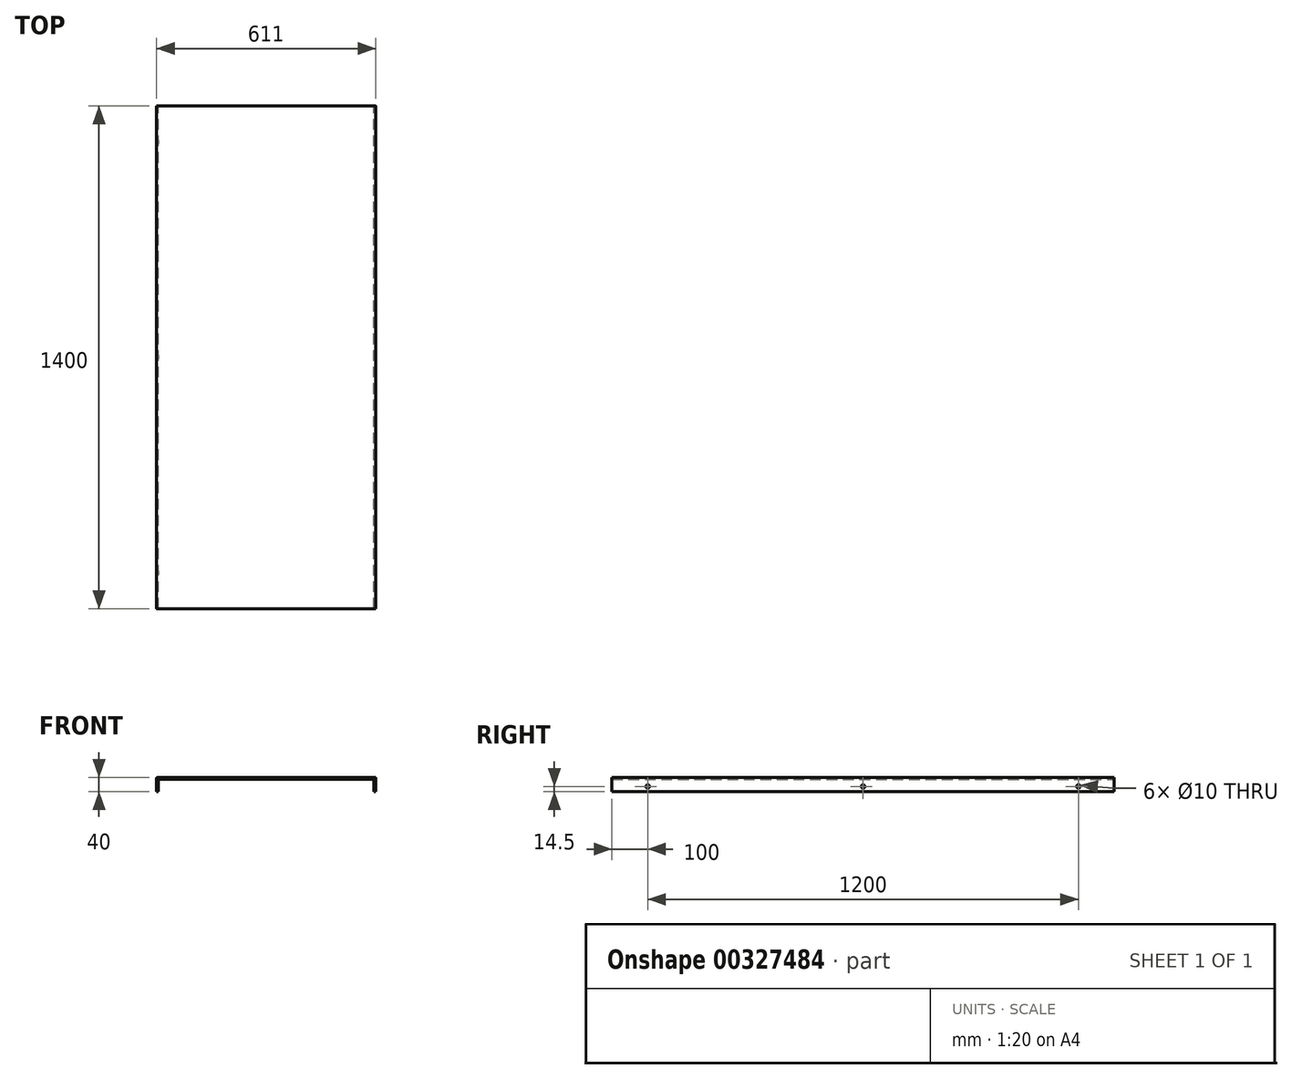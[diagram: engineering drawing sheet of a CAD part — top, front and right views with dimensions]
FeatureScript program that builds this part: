
annotation { "Feature Type Name" : "Feature", "Feature Type Description" : "" }
export const myFeature = defineFeature(function(context is Context, id is Id, definition is map)
    precondition{}
    {
        {
            var Q0;
            Q0=qCreatedBy(makeId("Front.planeOp"),FACE);
            var sketch = newSketch(context, id + "F0", { "sketchPlane" : qUnion([Q0])});
            skLineSegment(sketch, "E0", {"start": v(0, 0) * mm, "end": v(305.5, 0) * mm});
            skLineSegment(sketch, "E1", {"start": v(0, 0) * mm, "end": v(0, 40.14) * mm, "construction": true});
            skLineSegment(sketch, "E2.MirrorCS", {"start": v(0, 0) * mm, "end": v(-305.5, 0) * mm});
            skLineSegment(sketch, "E3", {"start": v(0, -5.5) * mm, "end": v(300, -5.5) * mm});
            skLineSegment(sketch, "E4", {"start": v(305.5, 0) * mm, "end": v(305.5, -40) * mm});
            skLineSegment(sketch, "E5.MirrorCS", {"start": v(-305.5, 0) * mm, "end": v(-305.5, -40) * mm});
            skLineSegment(sketch, "E6.MirrorCS", {"start": v(0, -5.5) * mm, "end": v(-300, -5.5) * mm});
            skLineSegment(sketch, "E7", {"start": v(300, -14.07) * mm, "end": v(300, -5.5) * mm});
            skLineSegment(sketch, "E8", {"start": v(300, -14.07) * mm, "end": v(300, -40) * mm});
            skLineSegment(sketch, "E9", {"start": v(305.5, -40) * mm, "end": v(300, -40) * mm});
            skLineSegment(sketch, "E10", {"start": v(-300, -5.5) * mm, "end": v(-300, -40) * mm});
            skLineSegment(sketch, "E11", {"start": v(-305.5, -40) * mm, "end": v(-300, -40) * mm});
            skSolve(sketch);
        }
        {
            var Q0;
            Q0 = qSketchRegion(id + "F0", true);
            extrude(context, id + "F1", {"entities" : qUnion([Q0]), "depth" : 1400 * mm});
        }
        {
            var Q0;
            Q0=makeQuery(id+"F1.opExtrude","SWEPT_FACE",FACE,{"disambiguationData":[OSD([sQuery(id+"F0.wireOp",EDGE,"E5.MirrorCS")])]});
            var sketch = newSketch(context, id + "F2", { "sketchPlane" : qUnion([Q0])});
            skCircle(sketch, "E12", {"center": v(100, -20) * mm, "radius": 5 * mm});
            skPoint(sketch, "E12.centerSnap0", {"position": v(0, -20) * mm});
            skCircle(sketch, "E13", {"center": v(1300, -20) * mm, "radius": 5 * mm});
            skPoint(sketch, "E13.centerSnap0", {"position": v(1400, -20) * mm});
            skLineSegment(sketch, "E14", {"start": v(99.77, 0) * mm, "end": v(99.77, -5.5) * mm});
            skLineSegment(sketch, "E15", {"start": v(99.77, -5.5) * mm, "end": v(1400, -5.5) * mm});
            skLineSegment(sketch, "E16.0", {"start": v(1400, 0) * mm, "end": v(1400, -40) * mm});
            skLineSegment(sketch, "E17", {"start": v(99.77, -5.5) * mm, "end": v(0, -5.5) * mm});
            skLineSegment(sketch, "E18.0", {"start": v(0, 0) * mm, "end": v(0, -40) * mm});
            skLineSegment(sketch, "E19", {"start": v(100, -20) * mm, "end": v(100, -25.5) * mm});
            skLineSegment(sketch, "E20", {"start": v(900, -20) * mm, "end": v(900, -25.5) * mm});
            skLineSegment(sketch, "E21", {"start": v(1300, -20) * mm, "end": v(1300, -25.5) * mm});
            skLineSegment(sketch, "E22", {"start": v(100, -25.5) * mm, "end": v(700, -25.5) * mm});
            skLineSegment(sketch, "E23", {"start": v(700, -25.5) * mm, "end": v(1300, -25.5) * mm});
            skSolve(sketch);
        }
        {
            var Q0;
            Q0=makeQuery(id+"F1.opExtrude","SWEPT_EDGE",EDGE,{"disambiguationData":[OSD([sQuery(id+"F0.wireOp",EDGE,"E2.MirrorCS"),sQuery(id+"F0.wireOp",EDGE,"E5.MirrorCS")])]});
            var Q1;
            Q1=makeQuery(id+"F1.opExtrude","SWEPT_EDGE",EDGE,{"disambiguationData":[OSD([sQuery(id+"F0.wireOp",EDGE,"E0"),sQuery(id+"F0.wireOp",EDGE,"E4")])]});
            fillet(context, id + "F3", {"entities" : qUnion([Q0, Q1]), "radius" : 3 * mm, "tangentPropagation" : true, "allowEdgeOverflow" : false});
        }
        {
            var Q0;
            Q0=sQuery(id+"F2.wireOp",VERTEX,"E19.end");
            var Q1;
            Q1=sQuery(id+"F2.wireOp",VERTEX,"E22.end");
            var Q2;
            Q2=sQuery(id+"F2.wireOp",VERTEX,"E21.end");
            var Q3;
            Q3=makeQuery(id+"F1.opExtrude","SWEPT_BODY",BODY,{"disambiguationData":[OSD([sQuery(id+"F0.wireOp",EDGE,"E0"),sQuery(id+"F0.wireOp",EDGE,"E2.MirrorCS"),sQuery(id+"F0.wireOp",EDGE,"E3"),sQuery(id+"F0.wireOp",EDGE,"E4"),sQuery(id+"F0.wireOp",EDGE,"E5.MirrorCS"),sQuery(id+"F0.wireOp",EDGE,"E6.MirrorCS"),sQuery(id+"F0.wireOp",EDGE,"E7"),sQuery(id+"F0.wireOp",EDGE,"E8"),sQuery(id+"F0.wireOp",EDGE,"E9"),sQuery(id+"F0.wireOp",EDGE,"E10"),sQuery(id+"F0.wireOp",EDGE,"E11")])]});
            hole(context, id + "F4", {"style" : HoleStyle.SIMPLE, "endStyle" : HoleEndStyle.BLIND, "holeDiameter" : 10 * mm, "holeDepth" : 3000 * mm, "tappedDepth" : 12 * mm, "tapClearance" : 3, "locations" : qUnion([Q0, Q1, Q2]), "scope" : qUnion([Q3]), "startStyle" : HoleStartStyle.PART});
        }
    });
